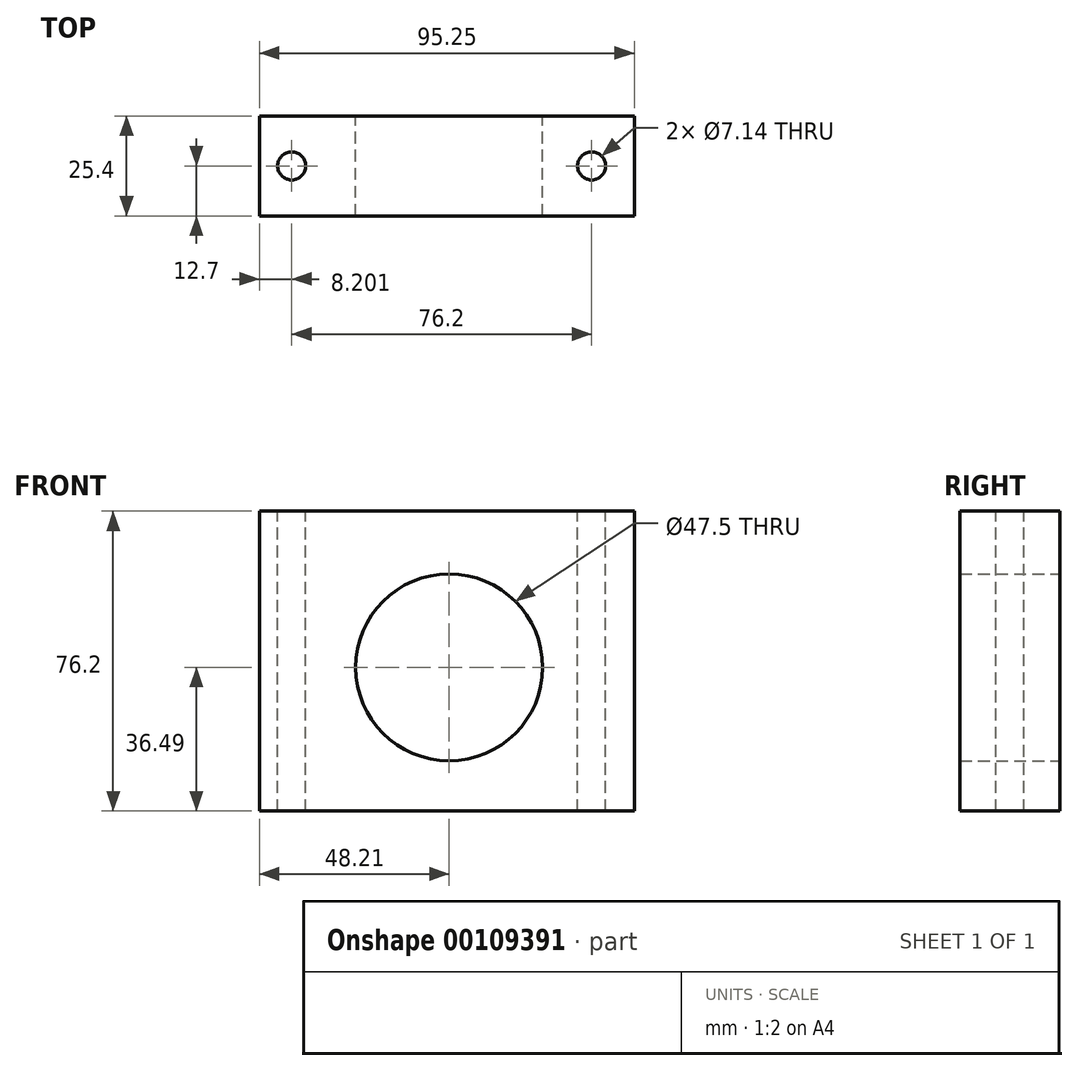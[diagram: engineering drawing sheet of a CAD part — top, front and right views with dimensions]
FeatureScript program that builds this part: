
annotation { "Feature Type Name" : "Feature", "Feature Type Description" : "" }
export const myFeature = defineFeature(function(context is Context, id is Id, definition is map)
    precondition{}
    {
        {
            var Q0;
            Q0=qCreatedBy(makeId("Front.planeOp"),FACE);
            var sketch = newSketch(context, id + "F0", { "sketchPlane" : qUnion([Q0])});
            skLineSegment(sketch, "E0", {"start": v(-48.21, 39.71) * mm, "end": v(47.04, 39.71) * mm});
            skLineSegment(sketch, "E1", {"start": v(47.04, 39.71) * mm, "end": v(47.04, -36.49) * mm});
            skLineSegment(sketch, "E2", {"start": v(47.04, -36.49) * mm, "end": v(-48.21, -36.49) * mm});
            skLineSegment(sketch, "E3", {"start": v(-48.21, -36.49) * mm, "end": v(-48.21, 39.71) * mm});
            skCircle(sketch, "E4", {"center": v(0, 0) * mm, "radius": 23.75 * mm});
            skSolve(sketch);
        }
        {
            var Q0;
            Q0 = qSketchRegion(id + "F0", true);
            extrude(context, id + "F1", {"entities" : qUnion([Q0]), "depth" : 25.4 * mm});
        }
        {
            var Q0;
            Q0=makeQuery(id+"F1.opExtrude","SWEPT_FACE",FACE,{"disambiguationData":[OSD([sQuery(id+"F0.wireOp",EDGE,"E0")])]});
            var sketch = newSketch(context, id + "F2", { "sketchPlane" : qUnion([Q0])});
            skCircle(sketch, "E5", {"center": v(-40, -12.7) * mm, "radius": 3.57 * mm});
            skCircle(sketch, "E6", {"center": v(36.2, -12.7) * mm, "radius": 3.57 * mm});
            skSolve(sketch);
        }
        {
            var Q0;
            Q0=makeQuery(id+"F2.imprint","IMPRINT",FACE,{"disambiguationData":[TD([[makeQuery(id+"F2.imprint","IMPRINT",EDGE,{"derivedFrom":sQuery(id+"F2.wireOp",EDGE,"E5")}),1.0]])]});
            var Q1;
            Q1=makeQuery(id+"F2.imprint","IMPRINT",FACE,{"disambiguationData":[TD([[makeQuery(id+"F2.imprint","IMPRINT",EDGE,{"derivedFrom":sQuery(id+"F2.wireOp",EDGE,"E6")}),1.0]])]});
            extrude(context, id + "F3", {"entities" : qUnion([Q0, Q1]), "operationType" : NewBodyOperationType.REMOVE, "endBound" : BoundingType.THROUGH_ALL, "oppositeDirection" : true, "depth" : 25.4 * mm});
        }
    });
